# Revit family: Faucet-Kitchen-KOHLER-Simplice-K-596ME_1
name_source: partatom
category: Plumbing Fixtures
units: mm (PartAtom-declared; Revit-internal decimal feet)

## family parameters
Cut with Voids When Loaded = No
Host = Face
OmniClass Number = 23.31.11.00
OmniClass Title = Faucets
Part Type = Normal
Room Calculation Point = No
Round Connector Dimension = Use Diameter
Shared = No

## types (1)
- BL-Matte Black
    ADA Compliant = No
    Assembly Code = D2010
    CW Connection = Yes
    Cold Water Inlet = Cold Water Inlet
    Date Modified = 05/01/2023
    Default Elevation = 36"
    Description = Single Hole or Three Hole Kitchen Faucet
    Drain Included = No
    Faucet Hole Spacing = 0"
    Finish = Kohler-Metal-BL-Matte_Black
    Flow Rate = 0 GPM
    HW Connection = Yes
    Handle Clearance = 3 1/16"
    Hot Water Inlet = Hot Water Inlet
    Length = 9 1/4"
    Manufacturer = Kohler Co.
    Master Format 2014 = 22 41 39
    Master Format 2014 Name = Residential Faucets, Supplies, and Trim
    Material = Premium Metal Construction
    Model = K-596ME-BL
    Pressure = 0.00 psi
    Product Name = Simplice
    Spout Reach = 9 1/4"
    Type = 1
    URL = https://me.kohler.com
    Vent Connection = No
    Waste Connection = No
    Waste Water Outlet = Waste Water Outlet
    WaterSense Certified = No

## geometry (parser evidence)
native form markers: Sweep x6
no freeform markers — native parametric forms only
